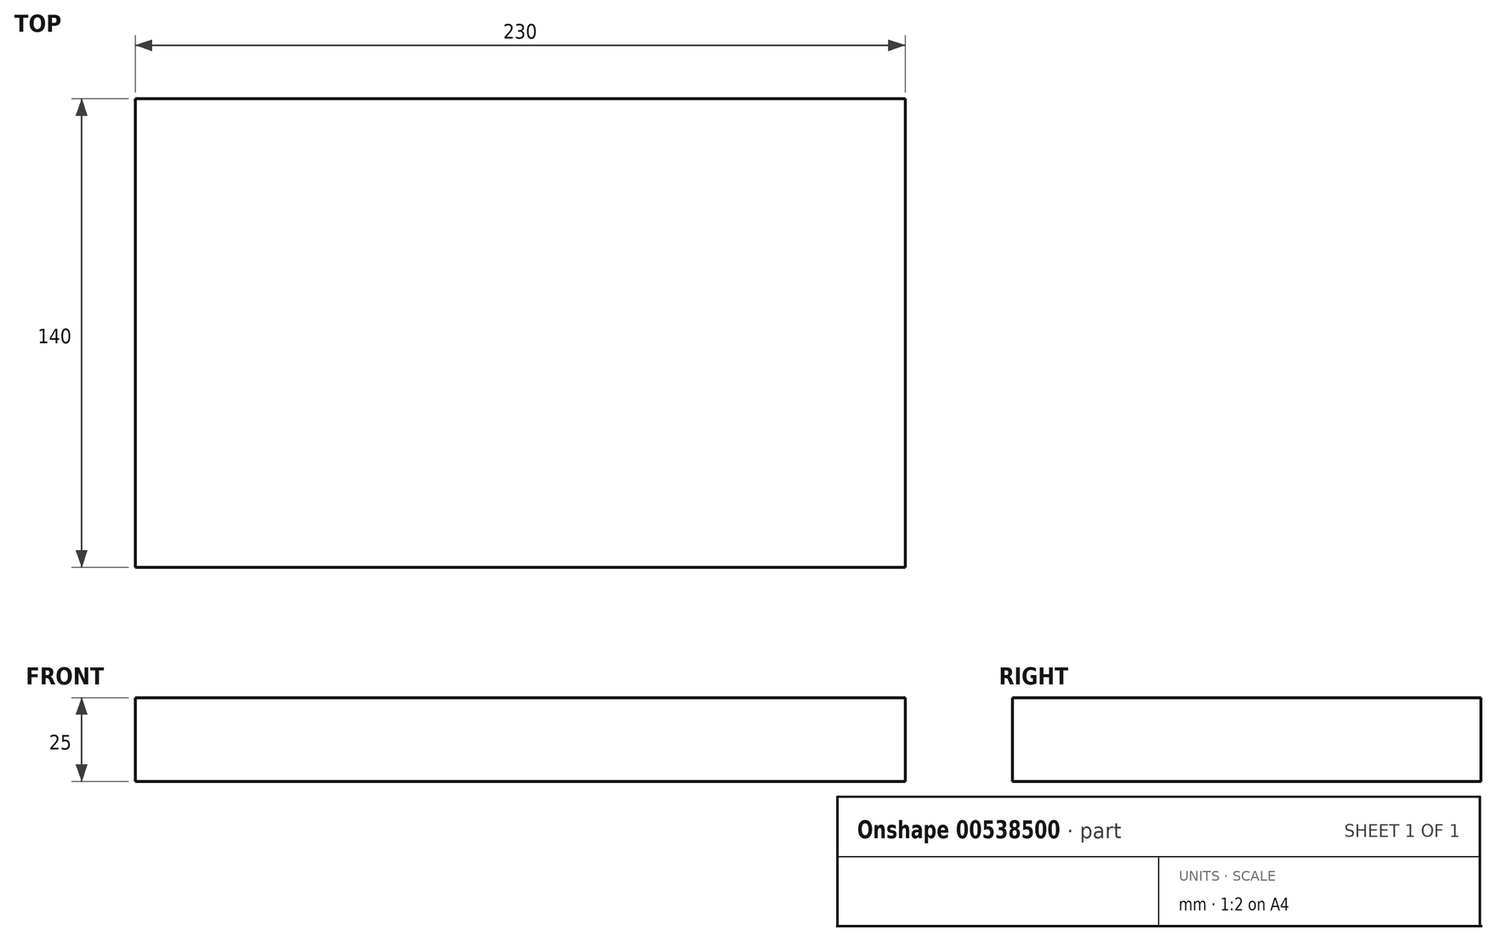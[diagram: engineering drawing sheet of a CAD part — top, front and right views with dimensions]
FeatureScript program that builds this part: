
annotation { "Feature Type Name" : "Feature", "Feature Type Description" : "" }
export const myFeature = defineFeature(function(context is Context, id is Id, definition is map)
    precondition{}
    {
        {
            var Q0;
            Q0=qCreatedBy(makeId("Top.planeOp"),FACE);
            var sketch = newSketch(context, id + "F0", { "sketchPlane" : qUnion([Q0])});
            skLineSegment(sketch, "E0.bottom", {"start": v(115, -70) * mm, "end": v(-115, -70) * mm});
            skLineSegment(sketch, "E0.top", {"start": v(115, 70) * mm, "end": v(-115, 70) * mm});
            skLineSegment(sketch, "E0.left", {"start": v(115, -70) * mm, "end": v(115, 70) * mm});
            skLineSegment(sketch, "E0.right", {"start": v(-115, -70) * mm, "end": v(-115, 70) * mm});
            skPoint(sketch, "E0.middle", {"position": v(0, 0) * mm});
            skSolve(sketch);
        }
        {
            var Q0;
            Q0=makeQuery(id+"F0.imprint","IMPRINT",FACE,{"disambiguationData":[TD([[makeQuery(id+"F0.imprint","IMPRINT",EDGE,{"derivedFrom":sQuery(id+"F0.wireOp",EDGE,"E0.bottom")}),-1.0]])]});
            extrude(context, id + "F1", {"entities" : qUnion([Q0]), "depth" : 25 * mm, "offsetDistance" : 25 * mm});
        }
    });
